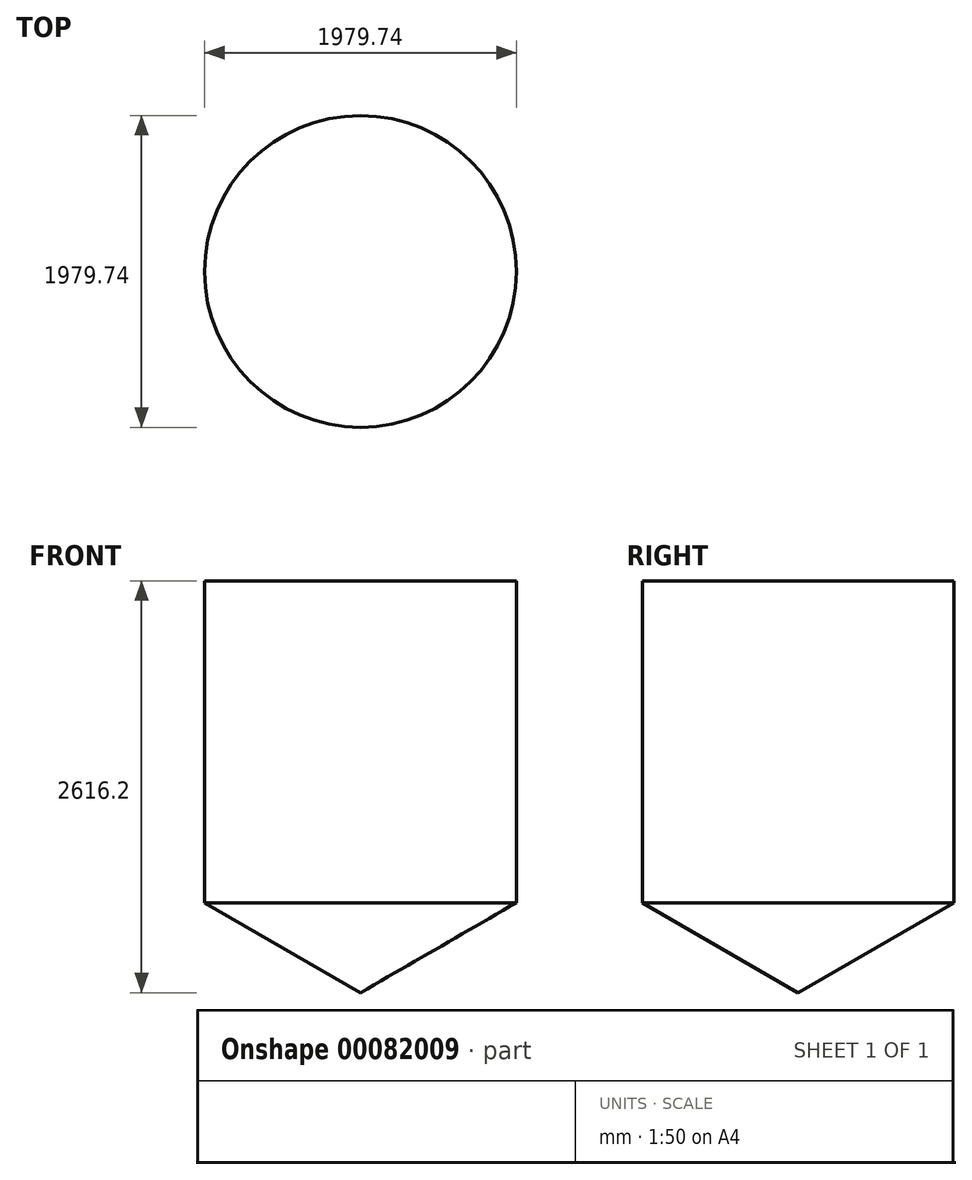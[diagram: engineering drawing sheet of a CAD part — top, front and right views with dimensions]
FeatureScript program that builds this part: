
annotation { "Feature Type Name" : "Feature", "Feature Type Description" : "" }
export const myFeature = defineFeature(function(context is Context, id is Id, definition is map)
    precondition{}
    {
        {
            var Q0;
            Q0=qCreatedBy(makeId("Front.planeOp"),FACE);
            var sketch = newSketch(context, id + "F0", { "sketchPlane" : qUnion([Q0])});
            skLineSegment(sketch, "E0", {"start": v(0, 0) * mm, "end": v(989.87, 571.5) * mm});
            skLineSegment(sketch, "E1", {"start": v(989.87, 571.5) * mm, "end": v(989.87, 2616.2) * mm});
            skLineSegment(sketch, "E2", {"start": v(989.87, 2616.2) * mm, "end": v(0, 2616.2) * mm});
            skLineSegment(sketch, "E3", {"start": v(0, 2616.2) * mm, "end": v(0, 0) * mm});
            skLineSegment(sketch, "E4", {"start": v(0, 3939.57) * mm, "end": v(0, 0) * mm, "construction": true});
            skSolve(sketch);
        }
        {
            var Q0;
            Q0=sQuery(id+"F0.wireOp",EDGE,"E2");
            var Q1;
            Q1=sQuery(id+"F0.wireOp",EDGE,"E1");
            var Q2;
            Q2=sQuery(id+"F0.wireOp",EDGE,"E0");
            var Q3;
            Q3=sQuery(id+"F0.wireOp",EDGE,"E4");
            revolve(context, id + "F1", {"bodyType" : ToolBodyType.SURFACE, "surfaceEntities" : qUnion([Q0, Q1, Q2]), "axis" : qUnion([Q3]), "revolveType" : RevolveType.FULL});
        }
    });
